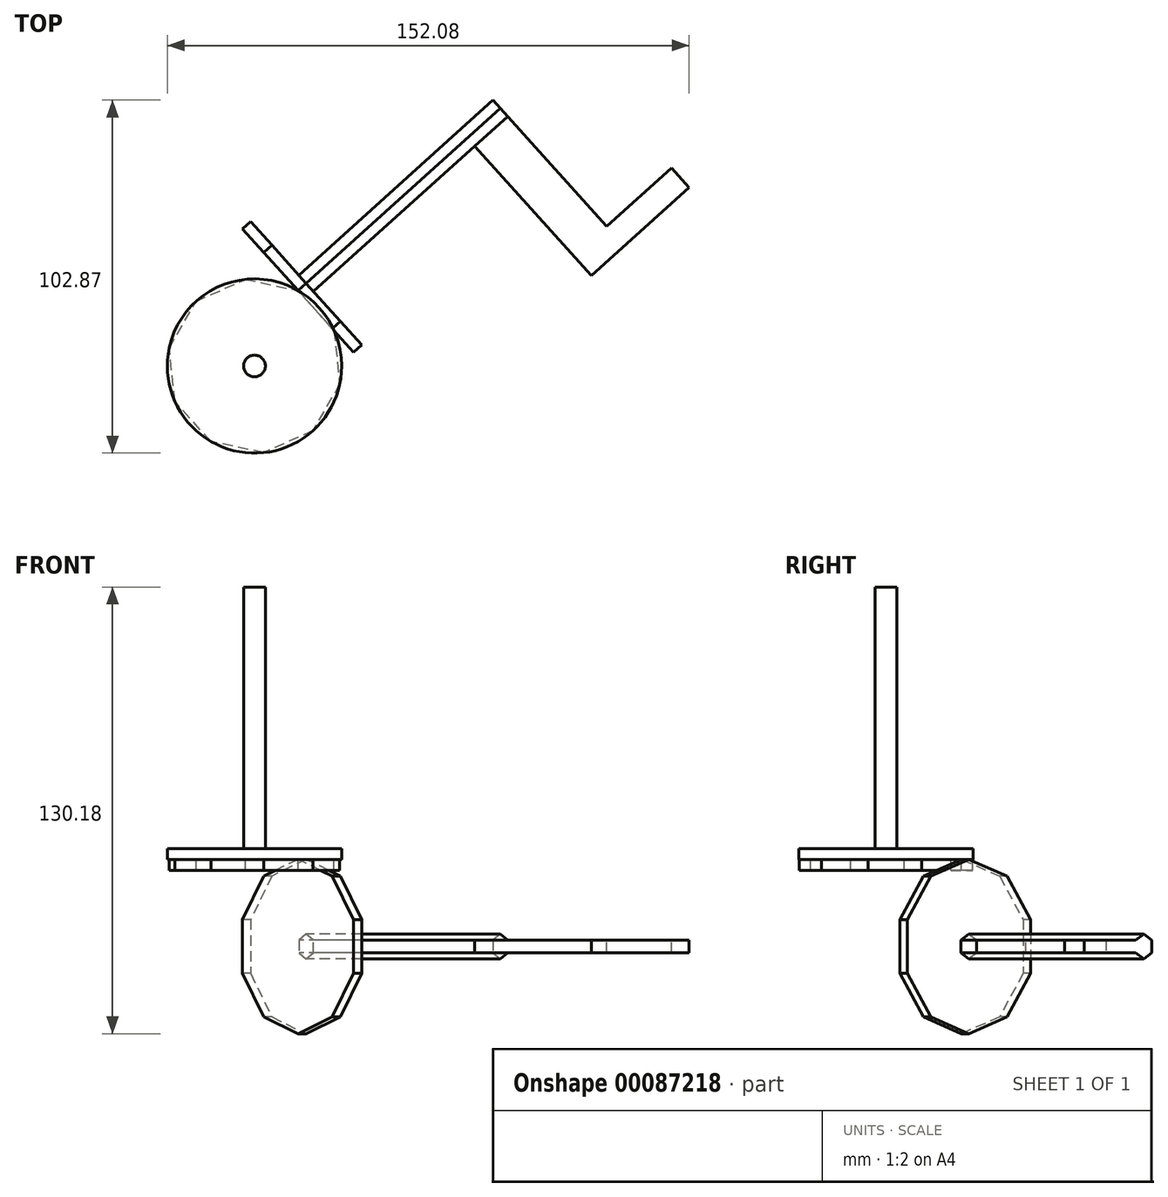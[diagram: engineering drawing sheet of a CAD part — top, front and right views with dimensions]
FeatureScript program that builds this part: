
annotation { "Feature Type Name" : "Feature", "Feature Type Description" : "" }
export const myFeature = defineFeature(function(context is Context, id is Id, definition is map)
    precondition{}
    {
        {
            var Q0;
            Q0=qCreatedBy(makeId("Top.planeOp"),FACE);
            var sketch = newSketch(context, id + "F0", { "sketchPlane" : qUnion([Q0])});
            skCircle(sketch, "E0", {"center": v(0, 0) * mm, "radius": 25.4 * mm});
            skSolve(sketch);
        }
        {
            var Q0;
            Q0=makeQuery(id+"F0.imprint","IMPRINT",FACE,{"disambiguationData":[TD([[makeQuery(id+"F0.imprint","IMPRINT",EDGE,{"derivedFrom":sQuery(id+"F0.wireOp",EDGE,"E0")}),1.0]])]});
            extrude(context, id + "F1", {"entities" : qUnion([Q0]), "depth" : 3.17 * mm});
        }
        {
            var Q0;
            Q0=makeQuery(id+"F1.opExtrude","CAP_FACE",FACE,{"disambiguationData":[OSD([sQuery(id+"F0.wireOp",EDGE,"E0")])],"isStart":false});
            var sketch = newSketch(context, id + "F2", { "sketchPlane" : qUnion([Q0])});
            skCircle(sketch, "E1", {"center": v(0, 0) * mm, "radius": 3.18 * mm});
            skSolve(sketch);
        }
        {
            var Q0;
            Q0 = qSketchRegion(id + "F2", true);
            extrude(context, id + "F3", {"entities" : qUnion([Q0]), "operationType" : NewBodyOperationType.ADD, "depth" : 76.2 * mm});
        }
        {
            var Q0;
            Q0=qCreatedBy(makeId("Top.planeOp"),FACE);
            var sketch = newSketch(context, id + "F4", { "sketchPlane" : qUnion([Q0])});
            skLineSegment(sketch, "E2", {"start": v(0, 0) * mm, "end": v(-25.4, 0) * mm});
            skCircle(sketch, "E3.0", {"center": v(0, 0) * mm, "radius": 25.4 * mm});
            skCircle(sketch, "E4.cCircle", {"center": v(0, 0) * mm, "radius": 25.4 * mm, "construction": true});
            skLineSegment(sketch, "E4.0", {"start": v(-24.84, 5.28) * mm, "end": v(-17, 18.88) * mm});
            skLineSegment(sketch, "E4.1", {"start": v(-17, 18.88) * mm, "end": v(-2.66, 25.26) * mm});
            skLineSegment(sketch, "E4.2", {"start": v(-2.66, 25.26) * mm, "end": v(12.7, 22) * mm});
            skLineSegment(sketch, "E4.3", {"start": v(12.7, 22) * mm, "end": v(23.2, 10.33) * mm});
            skLineSegment(sketch, "E4.4", {"start": v(23.2, 10.33) * mm, "end": v(24.84, -5.28) * mm});
            skLineSegment(sketch, "E4.5", {"start": v(24.84, -5.28) * mm, "end": v(17, -18.88) * mm});
            skLineSegment(sketch, "E4.6", {"start": v(17, -18.88) * mm, "end": v(2.66, -25.26) * mm});
            skLineSegment(sketch, "E4.7", {"start": v(2.66, -25.26) * mm, "end": v(-12.7, -22) * mm});
            skLineSegment(sketch, "E4.8", {"start": v(-12.7, -22) * mm, "end": v(-23.2, -10.33) * mm});
            skLineSegment(sketch, "E4.9", {"start": v(-23.2, -10.33) * mm, "end": v(-24.84, 5.28) * mm});
            skSolve(sketch);
        }
        {
            var Q0;
            Q0=makeQuery(id+"F4.imprint","IMPRINT",FACE,{"disambiguationData":[TD([[makeQuery(id+"F4.imprint","IMPRINT",EDGE,{"derivedFrom":sQuery(id+"F4.wireOp",EDGE,"E4.0")}),-1.0]])]});
            extrude(context, id + "F5", {"entities" : qUnion([Q0]), "operationType" : NewBodyOperationType.ADD, "oppositeDirection" : true, "depth" : 3.17 * mm});
        }
        {
            var Q0;
            Q0=makeQuery(id+"F5.opExtrude","SWEPT_FACE",FACE,{"disambiguationData":[OSD([sQuery(id+"F4.wireOp",EDGE,"E4.3")])]});
            var sketch = newSketch(context, id + "F6", { "sketchPlane" : qUnion([Q0])});
            skLineSegment(sketch, "E5", {"start": v(7.85, 0) * mm, "end": v(7.85, -25.4) * mm, "construction": true});
            skCircle(sketch, "E6.cCircle", {"center": v(7.85, -25.4) * mm, "radius": 25.4 * mm, "construction": true});
            skLineSegment(sketch, "E6.0", {"start": v(7.85, 0) * mm, "end": v(22.78, -4.85) * mm});
            skLineSegment(sketch, "E6.1", {"start": v(22.78, -4.85) * mm, "end": v(32, -17.55) * mm});
            skLineSegment(sketch, "E6.2", {"start": v(32, -17.55) * mm, "end": v(32, -33.25) * mm});
            skLineSegment(sketch, "E6.3", {"start": v(32, -33.25) * mm, "end": v(22.78, -45.95) * mm});
            skLineSegment(sketch, "E6.4", {"start": v(22.78, -45.95) * mm, "end": v(7.85, -50.8) * mm});
            skLineSegment(sketch, "E6.5", {"start": v(7.85, -50.8) * mm, "end": v(-7.08, -45.95) * mm});
            skLineSegment(sketch, "E6.6", {"start": v(-7.08, -45.95) * mm, "end": v(-16.3, -33.25) * mm});
            skLineSegment(sketch, "E6.7", {"start": v(-16.3, -33.25) * mm, "end": v(-16.3, -17.55) * mm});
            skLineSegment(sketch, "E6.8", {"start": v(-16.3, -17.55) * mm, "end": v(-7.08, -4.85) * mm});
            skLineSegment(sketch, "E6.9", {"start": v(-7.08, -4.85) * mm, "end": v(7.85, 0) * mm});
            skSolve(sketch);
        }
        {
            var Q0;
            Q0 = qSketchRegion(id + "F6", true);
            extrude(context, id + "F7", {"entities" : qUnion([Q0]), "operationType" : NewBodyOperationType.ADD, "depth" : 3.17 * mm});
        }
        {
            var Q0;
            Q0=makeQuery(id+"F7.opExtrude","CAP_FACE",FACE,{"disambiguationData":[OSD([sQuery(id+"F6.wireOp",EDGE,"E6.0"),sQuery(id+"F6.wireOp",EDGE,"E6.1"),sQuery(id+"F6.wireOp",EDGE,"E6.2"),sQuery(id+"F6.wireOp",EDGE,"E6.3"),sQuery(id+"F6.wireOp",EDGE,"E6.4"),sQuery(id+"F6.wireOp",EDGE,"E6.5"),sQuery(id+"F6.wireOp",EDGE,"E6.6"),sQuery(id+"F6.wireOp",EDGE,"E6.7"),sQuery(id+"F6.wireOp",EDGE,"E6.8"),sQuery(id+"F6.wireOp",EDGE,"E6.9")])],"isStart":false});
            var sketch = newSketch(context, id + "F8", { "sketchPlane" : qUnion([Q0])});
            skCircle(sketch, "E7.cCircle", {"center": v(7.85, -25.4) * mm, "radius": 3.67 * mm, "construction": true});
            skLineSegment(sketch, "E7.0", {"start": v(11.02, -23.57) * mm, "end": v(11.02, -27.23) * mm});
            skLineSegment(sketch, "E7.1", {"start": v(11.02, -27.23) * mm, "end": v(7.85, -29.07) * mm});
            skLineSegment(sketch, "E7.2", {"start": v(7.85, -29.07) * mm, "end": v(4.67, -27.23) * mm});
            skLineSegment(sketch, "E7.3", {"start": v(4.67, -27.23) * mm, "end": v(4.67, -23.57) * mm});
            skLineSegment(sketch, "E7.4", {"start": v(4.67, -23.57) * mm, "end": v(7.85, -21.73) * mm});
            skLineSegment(sketch, "E7.5", {"start": v(7.85, -21.73) * mm, "end": v(11.02, -23.57) * mm});
            skLineSegment(sketch, "E8", {"start": v(7.85, 0) * mm, "end": v(7.85, -50.8) * mm, "construction": true});
            skLineSegment(sketch, "E9", {"start": v(32, -25.4) * mm, "end": v(-16.3, -25.4) * mm, "construction": true});
            skSolve(sketch);
        }
        {
            var Q0;
            Q0=makeQuery(id+"F8.imprint","IMPRINT",FACE,{"disambiguationData":[TD([[makeQuery(id+"F8.imprint","IMPRINT",EDGE,{"derivedFrom":sQuery(id+"F8.wireOp",EDGE,"E7.0")}),-1.0]])]});
            extrude(context, id + "F9", {"entities" : qUnion([Q0]), "operationType" : NewBodyOperationType.ADD, "depth" : 76.2 * mm});
        }
        {
            var Q0;
            Q0=makeQuery(id+"F9.opExtrude","SWEPT_FACE",FACE,{"disambiguationData":[OSD([sQuery(id+"F8.wireOp",EDGE,"E7.3")])]});
            var sketch = newSketch(context, id + "F10", { "sketchPlane" : qUnion([Q0])});
            skLineSegment(sketch, "E10.bottom", {"start": v(103.53, -23.57) * mm, "end": v(90.64, -23.57) * mm});
            skLineSegment(sketch, "E10.top", {"start": v(103.53, -27.23) * mm, "end": v(90.64, -27.23) * mm});
            skLineSegment(sketch, "E10.left", {"start": v(103.53, -23.57) * mm, "end": v(103.53, -27.23) * mm});
            skLineSegment(sketch, "E10.right", {"start": v(90.64, -23.57) * mm, "end": v(90.64, -27.23) * mm});
            skSolve(sketch);
        }
        {
            var Q0;
            Q0=makeQuery(id+"F10.imprint","IMPRINT",FACE,{"disambiguationData":[TD([[makeQuery(id+"F10.imprint","IMPRINT",EDGE,{"derivedFrom":sQuery(id+"F10.wireOp",EDGE,"E10.bottom")}),1.0]])]});
            extrude(context, id + "F11", {"entities" : qUnion([Q0]), "operationType" : NewBodyOperationType.ADD, "depth" : 50.8 * mm});
        }
        {
            var Q0;
            Q0=makeQuery(id+"F11.boolean.opBoolean","MERGE",FACE,{"derivedFrom":[makeQuery(id+"F9.opExtrude","CAP_FACE",FACE,{"disambiguationData":[OSD([sQuery(id+"F8.wireOp",EDGE,"E7.0"),sQuery(id+"F8.wireOp",EDGE,"E7.1"),sQuery(id+"F8.wireOp",EDGE,"E7.2"),sQuery(id+"F8.wireOp",EDGE,"E7.3"),sQuery(id+"F8.wireOp",EDGE,"E7.4"),sQuery(id+"F8.wireOp",EDGE,"E7.5")])],"isStart":false}),makeQuery(id+"F11.opExtrude","SWEPT_FACE",FACE,{"disambiguationData":[OSD([sQuery(id+"F10.wireOp",EDGE,"E10.left")])]})]});
            var sketch = newSketch(context, id + "F12", { "sketchPlane" : qUnion([Q0])});
            skLineSegment(sketch, "E11.bottom", {"start": v(-38.41, -27.23) * mm, "end": v(-46.13, -27.23) * mm});
            skLineSegment(sketch, "E11.top", {"start": v(-38.41, -23.57) * mm, "end": v(-46.13, -23.57) * mm});
            skLineSegment(sketch, "E11.left", {"start": v(-38.41, -27.23) * mm, "end": v(-38.41, -23.57) * mm});
            skLineSegment(sketch, "E11.right", {"start": v(-46.13, -27.23) * mm, "end": v(-46.13, -23.57) * mm});
            skSolve(sketch);
        }
        {
            var Q0;
            Q0 = qSketchRegion(id + "F12", true);
            extrude(context, id + "F13", {"entities" : qUnion([Q0]), "operationType" : NewBodyOperationType.ADD, "depth" : 25.4 * mm});
        }
    });
